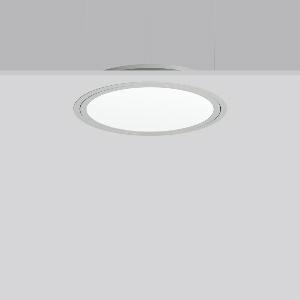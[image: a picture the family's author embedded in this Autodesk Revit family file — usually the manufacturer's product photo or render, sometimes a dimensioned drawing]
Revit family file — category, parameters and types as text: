
# Revit family: triona_round_e_312419_004_2_12_fb65
name_source: partatom
category: Lighting Fixtures
units: mm (PartAtom-declared; Revit-internal decimal feet)

## family parameters
Cut with Voids When Loaded = No
Host = Face
Light Source = No
Part Type = Normal
Room Calculation Point = No
Round Connector Dimension = Use Diameter
Shared = No

## types (1)
- TuneableWhite 846 (1 x LED Modul 846, 2450 lm, 4600)
    Apparent Load = 29 VA
    CIE Flux Codes = 48 80 96 100 100
    Color Rendering = 80
    Color Temperature = 4600
    Default Elevation = 1800 mm
    Description = Series: TRIONA round
Decorative round LED recessed surface luminaire. Cover made of sheet steel, powder-coated. Frame made of aluminium, powder-coated. Recessed ring: aluminium extrusion profile, powder coated. Light emission through a diffuser: plastic, opal. Lightguide and diffuser made of non-yellowing plastic (PMMA). Lateral light emission (RZB SIDELITE technology) for above-average homogeneous light distribution. Tunable white versions, dynamically adjustable from 2700 K to 6500 K. Suitable for installation in cavity ceilings. Tool-free mounting system thanks to the rocker arm mechanism (patent pending). Electronic ballast included. Very easy installation thanks to Plug+Play connection. Ideal for use as part of the Human Centric Lighting concept in connection with RZB light management systems. 
Colour: silver, matt (approx. RAL 9006)
Diameter: 505 mm
Height: 2 mm
Cut-out diameter: 482 mm
Recess height: 100 mm
Luminaire: recess height: 89 mm
Lamp: LED
Socket: without socket
Colour temperature: 2700K - 6500K
Colour rendering index (CRI): 80
System power: 29 W
Rated luminous flux: 2450 lm
Luminous efficiency: 84 lm/W
System power 2: 29 W
Rated luminous flux 2: 2350 lm
Luminous efficiency 2: 81 lm/W
System power 3: 30 W
Rated luminous flux 3: 2400 lm
Luminous efficiency 3: 80 lm/W
Control gear: Converter, dimmable, DALI
Protection class: I
Type of protection: IP 40
    Height = 0 mm  [stored 0 ft]
    Lamp = 1 x LED Modul 846
    Lamp Light Flux = 2450 lm
    Lamp count = 1
    Length = 505 mm
    Lifetime = 50000 h
    Luminous efficacy = 84 lm/W
    Manufacturer = RZB
    ModVariant = No
    Model = 312419.004.2.12
    Mounting Place = Ceiling
    Mounting Type = Recessed
    Number of Poles = 1
    OnlyDefault = Yes
    Power Factor = 1
    Product Name = TRIONA round E
    Product group = Recessed modular luminaires
    ProductGroupID = 406
    Protection Class = Protection class I
    Protection Degree = IP 20
    RLX_Detail_Level = 1
    RLX_Emergency_Light_Flux = 0 lm
    RLX_Emergency_Type = 0
    RLX_Emergency_Type_DB = No
    RlxData = <blob elided: 31873 chars, md5=cca4b28e>
    Socket = socket
    Standby Power = 0 W
    System Light Flux = 2450 lm
    System Power = 29 W
    Type Comments = TuneableWhite 846
    Type Image = 312419.004.12.jpg
    URL = http://relux.com
    VarID = tuneablewhite_846
    Voltage = 230 V
    Voltage Range = 220-240 V
    Weight = 0.00 kg
    Width = 0 mm  [stored 0 ft]

note: [stored X ft] marks values corroborated as IEEE doubles in the binary element streams (Revit-internal decimal feet)

## geometry (parser evidence)
native form markers: Blend x4, Sweep x10
no freeform markers — native parametric forms only
